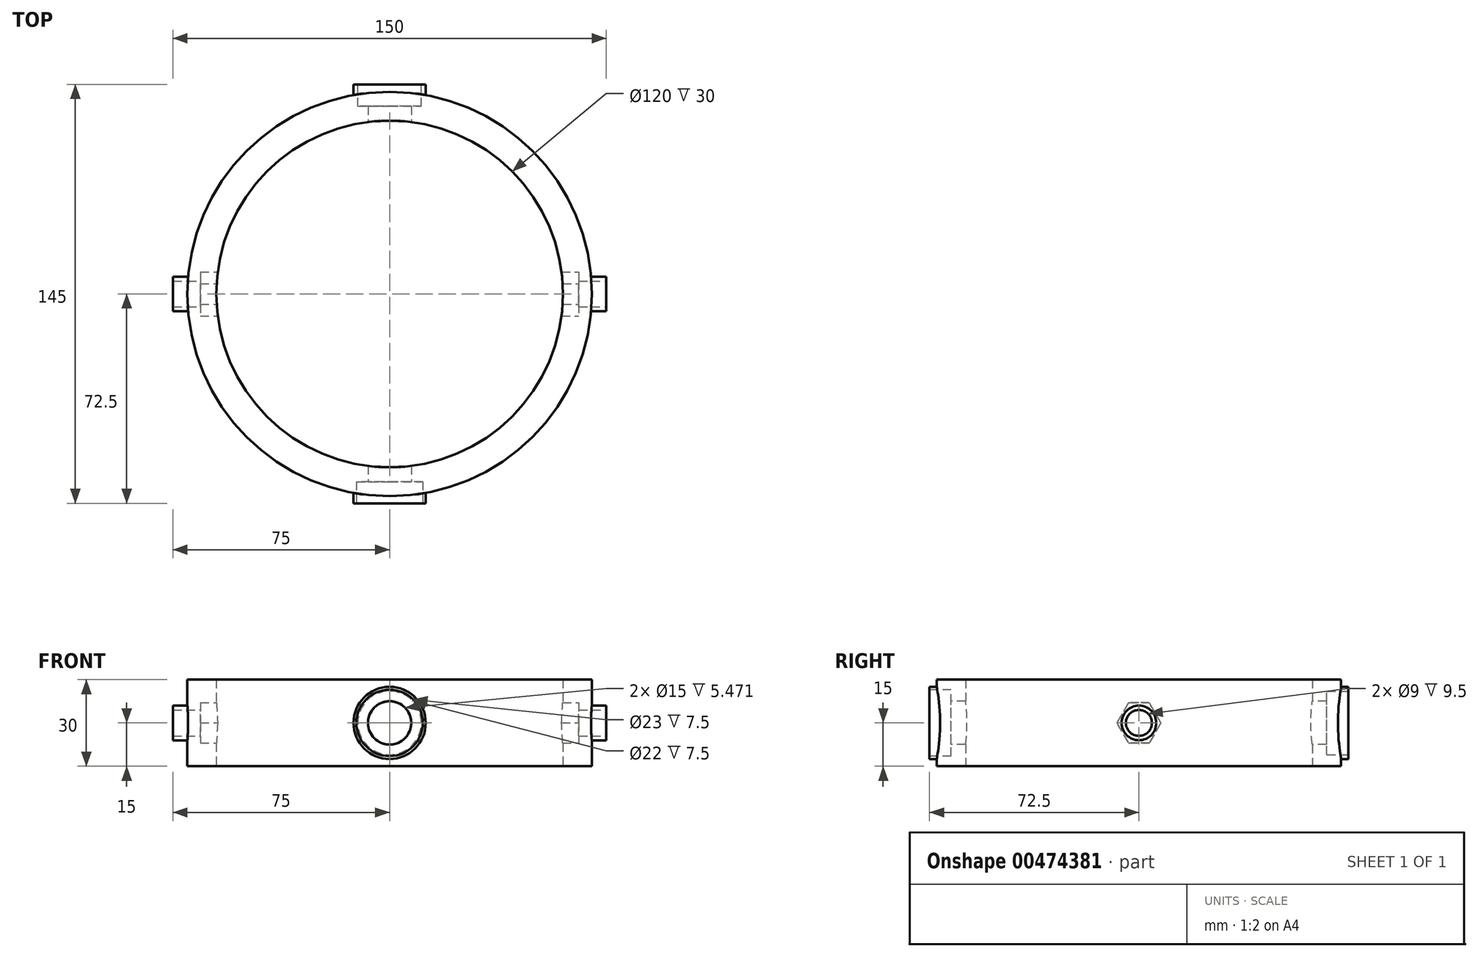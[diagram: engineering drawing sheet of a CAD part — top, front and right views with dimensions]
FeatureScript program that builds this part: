
annotation { "Feature Type Name" : "Feature", "Feature Type Description" : "" }
export const myFeature = defineFeature(function(context is Context, id is Id, definition is map)
    precondition{}
    {
        {
            var Q0;
            Q0=qCreatedBy(makeId("Top.planeOp"),FACE);
            var sketch = newSketch(context, id + "F0", { "sketchPlane" : qUnion([Q0])});
            skCircle(sketch, "E0", {"center": v(0, 0) * mm, "radius": 60 * mm});
            skCircle(sketch, "E1", {"center": v(0, 0) * mm, "radius": 70 * mm});
            skSolve(sketch);
        }
        {
            var Q0;
            Q0 = qSketchRegion(id + "F0", true);
            extrude(context, id + "F1", {"entities" : qUnion([Q0]), "depth" : 15 * mm, "hasSecondDirection" : true, "secondDirectionOppositeDirection" : true, "secondDirectionDepth" : 15 * mm});
        }
        {
            var Q0;
            Q0=qCreatedBy(makeId("Front.planeOp"),FACE);
            var sketch = newSketch(context, id + "F2", { "sketchPlane" : qUnion([Q0])});
            skCircle(sketch, "E2", {"center": v(0, 0) * mm, "radius": 7.5 * mm});
            skSolve(sketch);
        }
        {
            var Q0;
            Q0 = qSketchRegion(id + "F2", true);
            extrude(context, id + "F3", {"entities" : qUnion([Q0]), "operationType" : NewBodyOperationType.REMOVE, "endBound" : BoundingType.THROUGH_ALL, "oppositeDirection" : true, "depth" : 25 * mm, "hasSecondDirection" : true, "secondDirectionBound" : SecondDirectionBoundingType.THROUGH_ALL, "secondDirectionOppositeDirection" : false, "secondDirectionDepth" : 25 * mm});
        }
        {
            var Q0;
            Q0=qCreatedBy(makeId("Front.planeOp"),FACE);
            cPlane(context, id + "F4", {"entities" : qUnion([Q0]), "cplaneType" : CPlaneType.OFFSET, "offset" : 70 * mm, "width" : 150 * mm, "height" : 150 * mm});
        }
        {
            var Q0;
            Q0=qCreatedBy(makeId("Front.planeOp"),FACE);
            cPlane(context, id + "F5", {"entities" : qUnion([Q0]), "cplaneType" : CPlaneType.OFFSET, "offset" : 70 * mm, "oppositeDirection" : true, "width" : 150 * mm, "height" : 150 * mm});
        }
        {
            var Q0;
            Q0=qCreatedBy(id+"F4.planeOp",FACE);
            var sketch = newSketch(context, id + "F6", { "sketchPlane" : qUnion([Q0])});
            skCircle(sketch, "E3", {"center": v(0, 0) * mm, "radius": 11.5 * mm});
            skSolve(sketch);
        }
        {
            var Q0;
            Q0 = qSketchRegion(id + "F6", true);
            extrude(context, id + "F7", {"entities" : qUnion([Q0]), "operationType" : NewBodyOperationType.REMOVE, "oppositeDirection" : true, "depth" : 5 * mm});
        }
        {
            var Q0;
            Q0=qCreatedBy(id+"F5.planeOp",FACE);
            var sketch = newSketch(context, id + "F8", { "sketchPlane" : qUnion([Q0])});
            skCircle(sketch, "E4", {"center": v(0, 0) * mm, "radius": 11 * mm});
            skSolve(sketch);
        }
        {
            var Q0;
            Q0 = qSketchRegion(id + "F8", true);
            extrude(context, id + "F9", {"entities" : qUnion([Q0]), "operationType" : NewBodyOperationType.REMOVE, "depth" : 5 * mm});
        }
        {
            var Q0;
            Q0=qCreatedBy(id+"F4.planeOp",FACE);
            var sketch = newSketch(context, id + "F10", { "sketchPlane" : qUnion([Q0])});
            skCircle(sketch, "E5.0", {"center": v(0, 0) * mm, "radius": 11.5 * mm});
            skCircle(sketch, "E6", {"center": v(0, 0) * mm, "radius": 12.5 * mm});
            skSolve(sketch);
        }
        {
            var Q0;
            Q0 = qSketchRegion(id + "F10", true);
            var Q1;
            Q1=makeQuery(id+"F1.opExtrude","SWEPT_FACE",FACE,{"disambiguationData":[OSD([sQuery(id+"F0.wireOp",EDGE,"E1")])]});
            extrude(context, id + "F11", {"entities" : qUnion([Q0]), "operationType" : NewBodyOperationType.ADD, "depth" : 2.5 * mm, "hasSecondDirection" : true, "secondDirectionBound" : SecondDirectionBoundingType.UP_TO_SURFACE, "secondDirectionOppositeDirection" : true, "secondDirectionBoundEntityFace" : qUnion([Q1]), "secondDirectionDepth" : 25 * mm});
        }
        {
            var Q0;
            Q0=qCreatedBy(id+"F5.planeOp",FACE);
            var sketch = newSketch(context, id + "F12", { "sketchPlane" : qUnion([Q0])});
            skCircle(sketch, "E7", {"center": v(0, 0) * mm, "radius": 12.5 * mm});
            skCircle(sketch, "E8.0", {"center": v(0, 0) * mm, "radius": 11 * mm});
            skSolve(sketch);
        }
        {
            var Q0;
            Q0 = qSketchRegion(id + "F12", true);
            var Q1;
            Q1=makeQuery(id+"F1.opExtrude","SWEPT_FACE",FACE,{"disambiguationData":[OSD([sQuery(id+"F0.wireOp",EDGE,"E1")])]});
            extrude(context, id + "F13", {"entities" : qUnion([Q0]), "operationType" : NewBodyOperationType.ADD, "oppositeDirection" : true, "depth" : 2.5 * mm, "hasSecondDirection" : true, "secondDirectionBound" : SecondDirectionBoundingType.UP_TO_SURFACE, "secondDirectionOppositeDirection" : false, "secondDirectionBoundEntityFace" : qUnion([Q1]), "secondDirectionDepth" : 25 * mm});
        }
        {
            var Q0;
            Q0=qCreatedBy(makeId("Right.planeOp"),FACE);
            cPlane(context, id + "F14", {"entities" : qUnion([Q0]), "cplaneType" : CPlaneType.OFFSET, "offset" : 70 * mm, "width" : 150 * mm, "height" : 150 * mm});
        }
        {
            var Q0;
            Q0=qCreatedBy(id+"F14.planeOp",FACE);
            var sketch = newSketch(context, id + "F15", { "sketchPlane" : qUnion([Q0])});
            skCircle(sketch, "E9", {"center": v(0, 0) * mm, "radius": 6 * mm});
            skCircle(sketch, "E10", {"center": v(0, 0) * mm, "radius": 4.5 * mm});
            skSolve(sketch);
        }
        {
            var Q0;
            Q0=makeQuery(id+"F15.imprint","IMPRINT",FACE,{"disambiguationData":[TD([[makeQuery(id+"F15.imprint","IMPRINT",EDGE,{"derivedFrom":sQuery(id+"F15.wireOp",EDGE,"E10")}),1.0]])]});
            extrude(context, id + "F16", {"entities" : qUnion([Q0]), "operationType" : NewBodyOperationType.REMOVE, "endBound" : BoundingType.THROUGH_ALL, "oppositeDirection" : true, "depth" : 25 * mm});
        }
        {
            var Q0;
            Q0 = qSketchRegion(id + "F15", true);
            var Q1;
            Q1=makeQuery(id+"F1.opExtrude","SWEPT_FACE",FACE,{"disambiguationData":[OSD([sQuery(id+"F0.wireOp",EDGE,"E1")])]});
            extrude(context, id + "F17", {"entities" : qUnion([Q0]), "operationType" : NewBodyOperationType.ADD, "depth" : 5 * mm, "hasSecondDirection" : true, "secondDirectionBound" : SecondDirectionBoundingType.UP_TO_SURFACE, "secondDirectionOppositeDirection" : true, "secondDirectionBoundEntityFace" : qUnion([Q1]), "secondDirectionDepth" : 25 * mm});
        }
        {
            var Q0;
            Q0=qCreatedBy(makeId("Right.planeOp"),FACE);
            cPlane(context, id + "F18", {"entities" : qUnion([Q0]), "cplaneType" : CPlaneType.OFFSET, "offset" : 70 * mm, "oppositeDirection" : true, "width" : 150 * mm, "height" : 150 * mm});
        }
        {
            var Q0;
            Q0=qCreatedBy(id+"F18.planeOp",FACE);
            var sketch = newSketch(context, id + "F19", { "sketchPlane" : qUnion([Q0])});
            skCircle(sketch, "E11.0", {"center": v(0, 0) * mm, "radius": 4.5 * mm});
            skCircle(sketch, "E12.0", {"center": v(0, 0) * mm, "radius": 6 * mm});
            skSolve(sketch);
        }
        {
            var Q0;
            Q0 = qSketchRegion(id + "F19", true);
            var Q1;
            Q1=makeQuery(id+"F1.opExtrude","SWEPT_FACE",FACE,{"disambiguationData":[OSD([sQuery(id+"F0.wireOp",EDGE,"E1")])]});
            extrude(context, id + "F20", {"entities" : qUnion([Q0]), "operationType" : NewBodyOperationType.ADD, "oppositeDirection" : true, "depth" : 5 * mm, "hasSecondDirection" : true, "secondDirectionBound" : SecondDirectionBoundingType.UP_TO_SURFACE, "secondDirectionOppositeDirection" : false, "secondDirectionBoundEntityFace" : qUnion([Q1]), "secondDirectionDepth" : 25 * mm});
        }
        {
            var Q0;
            Q0=qCreatedBy(makeId("Right.planeOp"),FACE);
            var sketch = newSketch(context, id + "F21", { "sketchPlane" : qUnion([Q0])});
            skLineSegment(sketch, "E13", {"start": v(0, 0) * mm, "end": v(0, 7) * mm, "construction": true});
            skLineSegment(sketch, "E14", {"start": v(0, 7) * mm, "end": v(7.6, 7) * mm, "construction": true});
            skLineSegment(sketch, "E15", {"start": v(0, 7) * mm, "end": v(3.56, 7) * mm});
            skLineSegment(sketch, "E16", {"start": v(3.56, 7) * mm, "end": v(7.6, 0) * mm});
            skLineSegment(sketch, "E17", {"start": v(7.6, 0) * mm, "end": v(3.56, -7) * mm});
            skLineSegment(sketch, "E18", {"start": v(3.56, -7) * mm, "end": v(0, -7) * mm});
            skLineSegment(sketch, "E19.MirrorCS", {"start": v(-3.56, 7) * mm, "end": v(-7.6, 0) * mm});
            skLineSegment(sketch, "E20.MirrorCS", {"start": v(-7.6, 0) * mm, "end": v(-3.56, -7) * mm});
            skLineSegment(sketch, "E21.MirrorCS", {"start": v(-3.56, -7) * mm, "end": v(0, -7) * mm});
            skLineSegment(sketch, "E22", {"start": v(-3.56, 7) * mm, "end": v(0, 7) * mm});
            skSolve(sketch);
        }
        {
            var Q0;
            Q0 = qSketchRegion(id + "F21", true);
            extrude(context, id + "F22", {"entities" : qUnion([Q0]), "operationType" : NewBodyOperationType.REMOVE, "oppositeDirection" : true, "depth" : 65.5 * mm, "hasSecondDirection" : true, "secondDirectionOppositeDirection" : false, "secondDirectionDepth" : 65.5 * mm});
        }
    });
